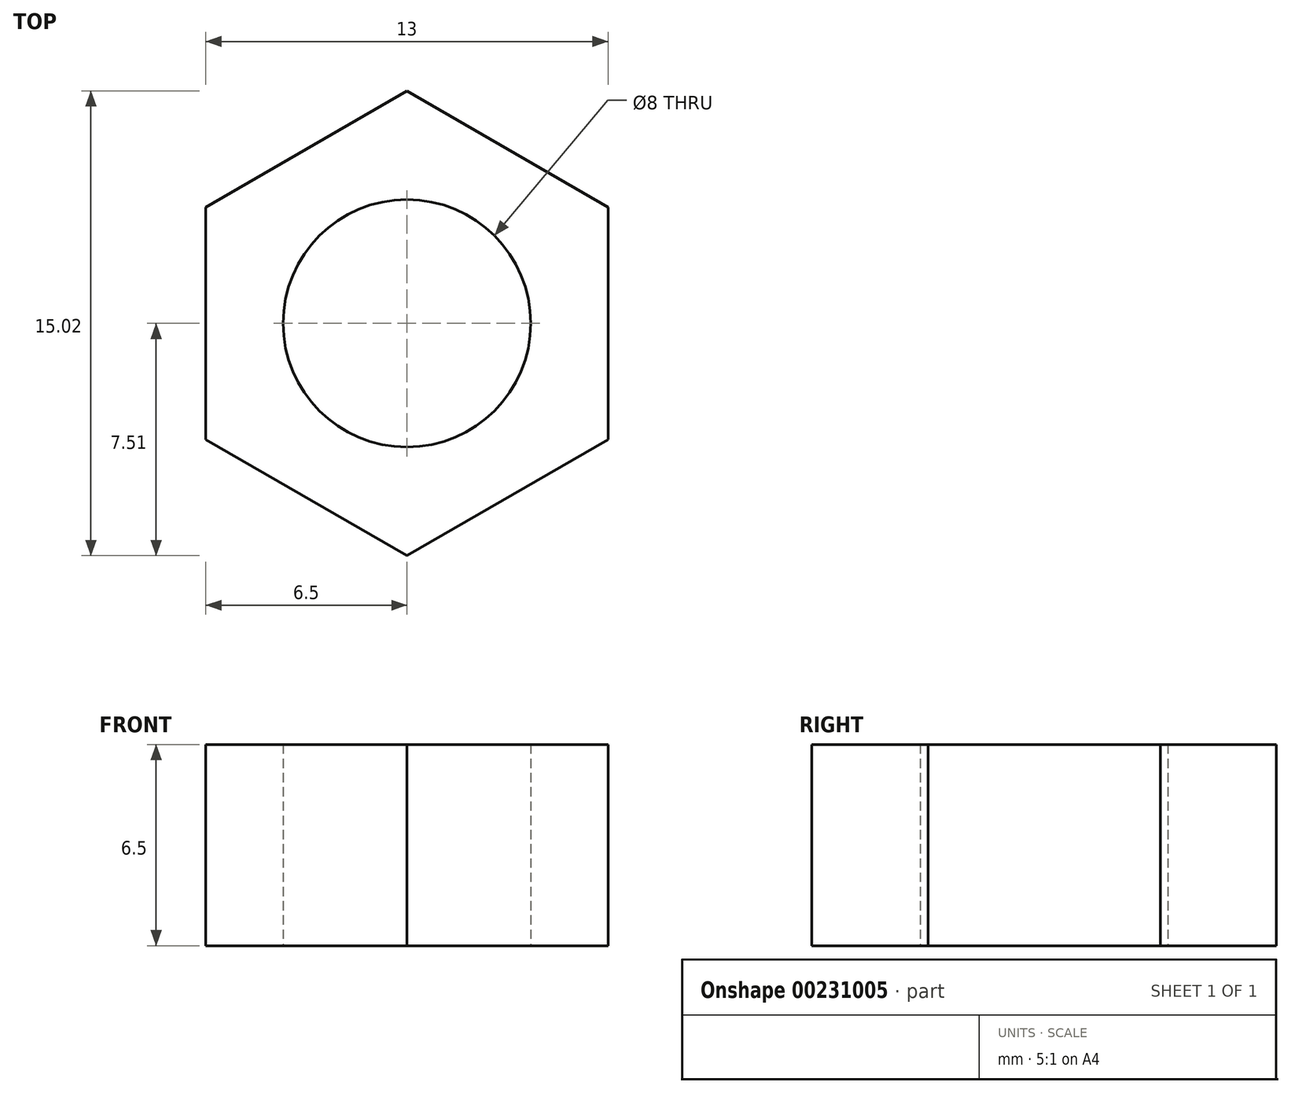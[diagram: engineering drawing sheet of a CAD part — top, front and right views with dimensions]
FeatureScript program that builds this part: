
annotation { "Feature Type Name" : "Feature", "Feature Type Description" : "" }
export const myFeature = defineFeature(function(context is Context, id is Id, definition is map)
    precondition{}
    {
        {
            var Q0;
            Q0=qCreatedBy(makeId("Top.planeOp"),FACE);
            var sketch = newSketch(context, id + "F0", { "sketchPlane" : qUnion([Q0])});
            skCircle(sketch, "E0.cCircle", {"center": v(0, 0) * mm, "radius": 7.5 * mm, "construction": true});
            skLineSegment(sketch, "E0.0", {"start": v(0, 7.5) * mm, "end": v(6.5, 3.75) * mm});
            skLineSegment(sketch, "E0.1", {"start": v(6.5, 3.75) * mm, "end": v(6.5, -3.75) * mm});
            skLineSegment(sketch, "E0.2", {"start": v(6.5, -3.75) * mm, "end": v(0, -7.5) * mm});
            skLineSegment(sketch, "E0.3", {"start": v(0, -7.5) * mm, "end": v(-6.5, -3.75) * mm});
            skLineSegment(sketch, "E0.4", {"start": v(-6.5, -3.75) * mm, "end": v(-6.5, 3.75) * mm});
            skLineSegment(sketch, "E0.5", {"start": v(-6.5, 3.75) * mm, "end": v(0, 7.5) * mm});
            skCircle(sketch, "E1", {"center": v(0, 0) * mm, "radius": 4 * mm});
            skSolve(sketch);
        }
        {
            var Q0;
            Q0=makeQuery(id+"F0.imprint","IMPRINT",FACE,{"disambiguationData":[TD([[makeQuery(id+"F0.imprint","IMPRINT",EDGE,{"derivedFrom":sQuery(id+"F0.wireOp",EDGE,"E0.0")}),-1.0]])]});
            extrude(context, id + "F1", {"entities" : qUnion([Q0]), "depth" : 6.5 * mm});
        }
    });
